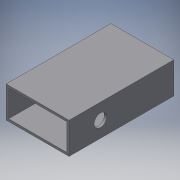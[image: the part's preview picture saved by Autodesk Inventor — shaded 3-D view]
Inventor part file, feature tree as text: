
AUTODESK INVENTOR PART (.ipt)
format: ipt  version: 2018 (Build 220112000, 112)  size: 104,448 bytes
history: native  units: mm
features: extrude x2, sketch x2, other x1
ambient origin geometry x8: Origin, YZ Plane, XZ Plane, XY Plane, X Axis, Y Axis, Z Axis, Center Point
bodies: Body1 (feature_tree)
feature tree (5):
  other  "ソリッド1"
  extrude  "押し出し1"  Depth=60.0mm
  extrude  "押し出し2"  Depth=30.0mm
  sketch  "スケッチ2"
  sketch  "スケッチ3"
